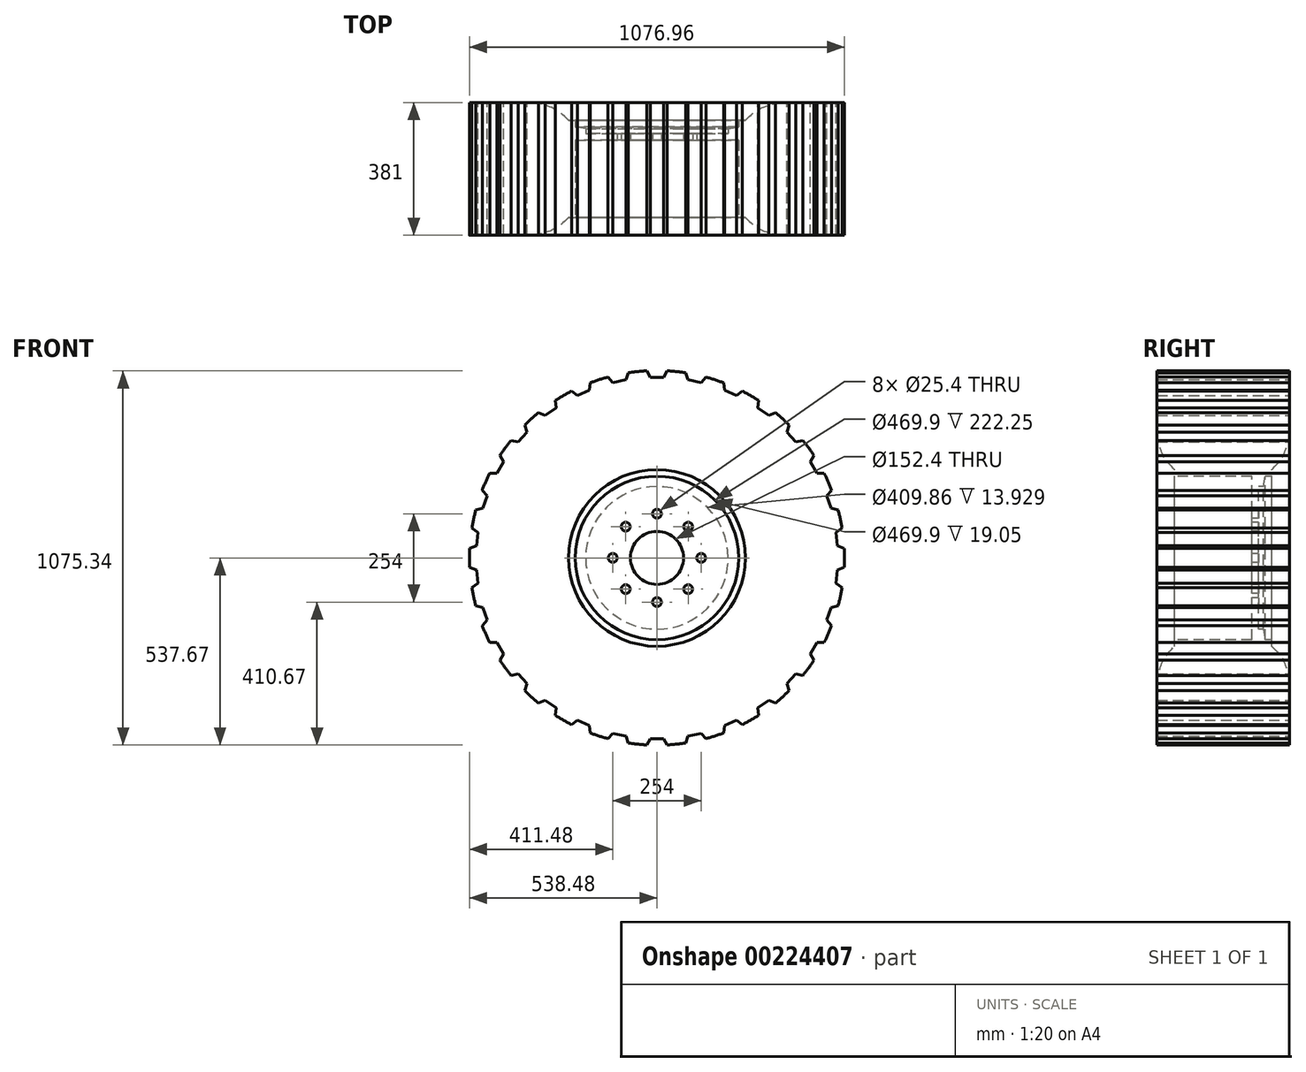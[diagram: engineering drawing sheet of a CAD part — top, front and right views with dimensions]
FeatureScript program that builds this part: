
annotation { "Feature Type Name" : "Feature", "Feature Type Description" : "" }
export const myFeature = defineFeature(function(context is Context, id is Id, definition is map)
    precondition{}
    {
        {
            var Q0;
            Q0=qCreatedBy(makeId("Top.planeOp"),FACE);
            var sketch = newSketch(context, id + "F0", { "sketchPlane" : qUnion([Q0])});
            skLineSegment(sketch, "E0", {"start": v(-538.48, 190.5) * mm, "end": v(-538.48, -190.5) * mm});
            skLineSegment(sketch, "E1", {"start": v(-538.48, -190.5) * mm, "end": v(-367.6, -190.5) * mm});
            skLineSegment(sketch, "E2", {"start": v(-538.48, 190.5) * mm, "end": v(-367.6, 190.5) * mm});
            skLineSegment(sketch, "E3", {"start": v(0, 0) * mm, "end": v(0, 343.31) * mm, "construction": true});
            skArc(sketch, "E4", {"start": v(-254, 139.7) * mm, "mid": v(-305.38, 177.22) * mm, "end": v(-367.6, 190.5) * mm});
            skArc(sketch, "E5", {"start": v(-367.6, -190.5) * mm, "mid": v(-305.38, -177.22) * mm, "end": v(-254, -139.7) * mm});
            skLineSegment(sketch, "E6", {"start": v(0, 0) * mm, "end": v(-538.48, 0) * mm, "construction": true});
            skLineSegment(sketch, "E7", {"start": v(-254, 139.7) * mm, "end": v(-254, -139.7) * mm});
            skLineSegment(sketch, "E8", {"start": v(-254, 139.7) * mm, "end": v(-234.95, 139.7) * mm});
            skLineSegment(sketch, "E9", {"start": v(-234.95, 139.7) * mm, "end": v(-234.95, 101.6) * mm});
            skLineSegment(sketch, "E10", {"start": v(-234.95, 101.6) * mm, "end": v(-76.2, 101.6) * mm});
            skLineSegment(sketch, "E11", {"start": v(-76.2, 101.6) * mm, "end": v(-76.2, 82.55) * mm});
            skLineSegment(sketch, "E12", {"start": v(-76.2, 82.55) * mm, "end": v(-234.95, 82.55) * mm});
            skLineSegment(sketch, "E13", {"start": v(-234.95, 82.55) * mm, "end": v(-234.95, -139.7) * mm});
            skLineSegment(sketch, "E14", {"start": v(-234.95, -139.7) * mm, "end": v(-254, -139.7) * mm});
            skLineSegment(sketch, "E15", {"start": v(-234.95, 120.65) * mm, "end": v(-204.93, 115.53) * mm});
            skLineSegment(sketch, "E16", {"start": v(-204.93, 115.53) * mm, "end": v(-204.93, 101.6) * mm});
            skSolve(sketch);
        }
        {
            var Q0;
            Q0 = qSketchRegion(id + "F0", true);
            var Q1;
            Q1=sQuery(id+"F0.wireOp",EDGE,"E3");
            revolve(context, id + "F1", {"entities" : qUnion([Q0]), "axis" : qUnion([Q1]), "revolveType" : RevolveType.FULL});
        }
        {
            var Q0;
            Q0=makeQuery(id+"F1.opRevolve","SWEPT_FACE",FACE,{"disambiguationData":[OSD([sQuery(id+"F0.wireOp",EDGE,"E1")])]});
            var sketch = newSketch(context, id + "F2", { "sketchPlane" : qUnion([Q0])});
            skCircle(sketch, "E17", {"center": v(0, 127) * mm, "radius": 12.7 * mm});
            skCircle(sketch, "E18.1.0", {"center": v(-89.8, 89.8) * mm, "radius": 12.7 * mm});
            skCircle(sketch, "E18.2.0", {"center": v(-127, 0) * mm, "radius": 12.7 * mm});
            skCircle(sketch, "E18.3.0", {"center": v(-89.8, -89.8) * mm, "radius": 12.7 * mm});
            skCircle(sketch, "E18.4.0", {"center": v(0, -127) * mm, "radius": 12.7 * mm});
            skCircle(sketch, "E18.5.0", {"center": v(89.8, -89.8) * mm, "radius": 12.7 * mm});
            skCircle(sketch, "E18.6.0", {"center": v(127, 0) * mm, "radius": 12.7 * mm});
            skCircle(sketch, "E18.7.0", {"center": v(89.8, 89.8) * mm, "radius": 12.7 * mm});
            skPoint(sketch, "E18.center", {"position": v(0, 0) * mm});
            skSolve(sketch);
        }
        {
            var Q0;
            Q0 = qSketchRegion(id + "F2", true);
            extrude(context, id + "F3", {"entities" : qUnion([Q0]), "operationType" : NewBodyOperationType.REMOVE, "endBound" : BoundingType.THROUGH_ALL, "oppositeDirection" : true, "depth" : 25.4 * mm});
        }
        {
            var Q0;
            Q0=makeQuery(id+"F1.opRevolve","SWEPT_FACE",FACE,{"disambiguationData":[OSD([sQuery(id+"F0.wireOp",EDGE,"E2")])]});
            var sketch = newSketch(context, id + "F4", { "sketchPlane" : qUnion([Q0])});
            skLineSegment(sketch, "E19", {"start": v(-29.58, 537.67) * mm, "end": v(-19.05, 519.43) * mm});
            skLineSegment(sketch, "E20", {"start": v(-19.05, 519.43) * mm, "end": v(19.05, 519.43) * mm});
            skLineSegment(sketch, "E21", {"start": v(19.05, 519.43) * mm, "end": v(29.58, 537.67) * mm});
            skArc(sketch, "E22.0", {"start": v(29.58, 537.67) * mm, "mid": v(0, 538.48) * mm, "end": v(-29.58, 537.67) * mm});
            skLineSegment(sketch, "E23", {"start": v(0, 519.43) * mm, "end": v(0, 0) * mm, "construction": true});
            skLineSegment(sketch, "E24.1.0", {"start": v(-140.72, 519.77) * mm, "end": v(-126.63, 504.12) * mm});
            skLineSegment(sketch, "E24.1.1", {"start": v(-126.63, 504.12) * mm, "end": v(-89.36, 512.04) * mm});
            skLineSegment(sketch, "E24.1.2", {"start": v(-89.36, 512.04) * mm, "end": v(-82.85, 532.07) * mm});
            skArc(sketch, "E24.1.3", {"start": v(-82.85, 532.07) * mm, "mid": v(-111.96, 526.71) * mm, "end": v(-140.72, 519.77) * mm});
            skLineSegment(sketch, "E24.2.0", {"start": v(-245.71, 479.15) * mm, "end": v(-228.67, 466.77) * mm});
            skLineSegment(sketch, "E24.2.1", {"start": v(-228.67, 466.77) * mm, "end": v(-193.87, 482.27) * mm});
            skLineSegment(sketch, "E24.2.2", {"start": v(-193.87, 482.27) * mm, "end": v(-191.67, 503.21) * mm});
            skArc(sketch, "E24.2.3", {"start": v(-191.67, 503.21) * mm, "mid": v(-219.02, 491.93) * mm, "end": v(-245.71, 479.15) * mm});
            skLineSegment(sketch, "E24.3.0", {"start": v(-339.96, 417.6) * mm, "end": v(-320.73, 409.03) * mm});
            skLineSegment(sketch, "E24.3.1", {"start": v(-320.73, 409.03) * mm, "end": v(-289.9, 431.43) * mm});
            skLineSegment(sketch, "E24.3.2", {"start": v(-289.9, 431.43) * mm, "end": v(-292.1, 452.37) * mm});
            skArc(sketch, "E24.3.3", {"start": v(-292.1, 452.37) * mm, "mid": v(-316.51, 435.64) * mm, "end": v(-339.96, 417.6) * mm});
            skLineSegment(sketch, "E24.4.0", {"start": v(-419.36, 337.79) * mm, "end": v(-398.76, 333.4) * mm});
            skLineSegment(sketch, "E24.4.1", {"start": v(-398.76, 333.4) * mm, "end": v(-373.26, 361.72) * mm});
            skLineSegment(sketch, "E24.4.2", {"start": v(-373.26, 361.72) * mm, "end": v(-379.77, 381.75) * mm});
            skArc(sketch, "E24.4.3", {"start": v(-379.77, 381.75) * mm, "mid": v(-400.17, 360.31) * mm, "end": v(-419.36, 337.79) * mm});
            skLineSegment(sketch, "E24.5.0", {"start": v(-480.42, 243.22) * mm, "end": v(-459.36, 243.22) * mm});
            skLineSegment(sketch, "E24.5.1", {"start": v(-459.36, 243.22) * mm, "end": v(-440.31, 276.21) * mm});
            skLineSegment(sketch, "E24.5.2", {"start": v(-440.31, 276.21) * mm, "end": v(-450.84, 294.45) * mm});
            skArc(sketch, "E24.5.3", {"start": v(-450.84, 294.45) * mm, "mid": v(-466.34, 269.24) * mm, "end": v(-480.42, 243.22) * mm});
            skLineSegment(sketch, "E24.6.0", {"start": v(-520.5, 138.02) * mm, "end": v(-499.9, 142.4) * mm});
            skLineSegment(sketch, "E24.6.1", {"start": v(-499.9, 142.4) * mm, "end": v(-488.12, 178.63) * mm});
            skLineSegment(sketch, "E24.6.2", {"start": v(-488.12, 178.63) * mm, "end": v(-502.21, 194.28) * mm});
            skArc(sketch, "E24.6.3", {"start": v(-502.21, 194.28) * mm, "mid": v(-512.12, 166.4) * mm, "end": v(-520.5, 138.02) * mm});
            skLineSegment(sketch, "E24.7.0", {"start": v(-537.81, 26.78) * mm, "end": v(-518.58, 35.35) * mm});
            skLineSegment(sketch, "E24.7.1", {"start": v(-518.58, 35.35) * mm, "end": v(-514.6, 73.24) * mm});
            skLineSegment(sketch, "E24.7.2", {"start": v(-514.6, 73.24) * mm, "end": v(-531.63, 85.62) * mm});
            skArc(sketch, "E24.7.3", {"start": v(-531.63, 85.62) * mm, "mid": v(-535.53, 56.29) * mm, "end": v(-537.81, 26.78) * mm});
            skLineSegment(sketch, "E24.8.0", {"start": v(-531.63, -85.62) * mm, "end": v(-514.6, -73.24) * mm});
            skLineSegment(sketch, "E24.8.1", {"start": v(-514.6, -73.24) * mm, "end": v(-518.58, -35.35) * mm});
            skLineSegment(sketch, "E24.8.2", {"start": v(-518.58, -35.35) * mm, "end": v(-537.81, -26.78) * mm});
            skArc(sketch, "E24.8.3", {"start": v(-537.81, -26.78) * mm, "mid": v(-535.53, -56.29) * mm, "end": v(-531.63, -85.62) * mm});
            skLineSegment(sketch, "E24.9.0", {"start": v(-502.21, -194.28) * mm, "end": v(-488.12, -178.63) * mm});
            skLineSegment(sketch, "E24.9.1", {"start": v(-488.12, -178.63) * mm, "end": v(-499.9, -142.4) * mm});
            skLineSegment(sketch, "E24.9.2", {"start": v(-499.9, -142.4) * mm, "end": v(-520.5, -138.02) * mm});
            skArc(sketch, "E24.9.3", {"start": v(-520.5, -138.02) * mm, "mid": v(-512.12, -166.4) * mm, "end": v(-502.21, -194.28) * mm});
            skLineSegment(sketch, "E24.10.0", {"start": v(-450.84, -294.45) * mm, "end": v(-440.31, -276.21) * mm});
            skLineSegment(sketch, "E24.10.1", {"start": v(-440.31, -276.21) * mm, "end": v(-459.36, -243.22) * mm});
            skLineSegment(sketch, "E24.10.2", {"start": v(-459.36, -243.22) * mm, "end": v(-480.42, -243.22) * mm});
            skArc(sketch, "E24.10.3", {"start": v(-480.42, -243.22) * mm, "mid": v(-466.34, -269.24) * mm, "end": v(-450.84, -294.45) * mm});
            skLineSegment(sketch, "E24.11.0", {"start": v(-379.77, -381.75) * mm, "end": v(-373.26, -361.72) * mm});
            skLineSegment(sketch, "E24.11.1", {"start": v(-373.26, -361.72) * mm, "end": v(-398.76, -333.4) * mm});
            skLineSegment(sketch, "E24.11.2", {"start": v(-398.76, -333.4) * mm, "end": v(-419.36, -337.79) * mm});
            skArc(sketch, "E24.11.3", {"start": v(-419.36, -337.79) * mm, "mid": v(-400.17, -360.31) * mm, "end": v(-379.77, -381.75) * mm});
            skLineSegment(sketch, "E24.12.0", {"start": v(-292.1, -452.37) * mm, "end": v(-289.9, -431.43) * mm});
            skLineSegment(sketch, "E24.12.1", {"start": v(-289.9, -431.43) * mm, "end": v(-320.73, -409.03) * mm});
            skLineSegment(sketch, "E24.12.2", {"start": v(-320.73, -409.03) * mm, "end": v(-339.96, -417.6) * mm});
            skArc(sketch, "E24.12.3", {"start": v(-339.96, -417.6) * mm, "mid": v(-316.51, -435.64) * mm, "end": v(-292.1, -452.37) * mm});
            skLineSegment(sketch, "E24.13.0", {"start": v(-191.67, -503.21) * mm, "end": v(-193.87, -482.27) * mm});
            skLineSegment(sketch, "E24.13.1", {"start": v(-193.87, -482.27) * mm, "end": v(-228.67, -466.77) * mm});
            skLineSegment(sketch, "E24.13.2", {"start": v(-228.67, -466.77) * mm, "end": v(-245.71, -479.15) * mm});
            skArc(sketch, "E24.13.3", {"start": v(-245.71, -479.15) * mm, "mid": v(-219.02, -491.93) * mm, "end": v(-191.67, -503.21) * mm});
            skLineSegment(sketch, "E24.14.0", {"start": v(-82.85, -532.07) * mm, "end": v(-89.36, -512.04) * mm});
            skLineSegment(sketch, "E24.14.1", {"start": v(-89.36, -512.04) * mm, "end": v(-126.63, -504.12) * mm});
            skLineSegment(sketch, "E24.14.2", {"start": v(-126.63, -504.12) * mm, "end": v(-140.72, -519.77) * mm});
            skArc(sketch, "E24.14.3", {"start": v(-140.72, -519.77) * mm, "mid": v(-111.96, -526.71) * mm, "end": v(-82.85, -532.07) * mm});
            skLineSegment(sketch, "E24.15.0", {"start": v(29.58, -537.67) * mm, "end": v(19.05, -519.43) * mm});
            skLineSegment(sketch, "E24.15.1", {"start": v(19.05, -519.43) * mm, "end": v(-19.05, -519.43) * mm});
            skLineSegment(sketch, "E24.15.2", {"start": v(-19.05, -519.43) * mm, "end": v(-29.58, -537.67) * mm});
            skArc(sketch, "E24.15.3", {"start": v(-29.58, -537.67) * mm, "mid": v(0, -538.48) * mm, "end": v(29.58, -537.67) * mm});
            skLineSegment(sketch, "E24.16.0", {"start": v(140.72, -519.77) * mm, "end": v(126.63, -504.12) * mm});
            skLineSegment(sketch, "E24.16.1", {"start": v(126.63, -504.12) * mm, "end": v(89.36, -512.04) * mm});
            skLineSegment(sketch, "E24.16.2", {"start": v(89.36, -512.04) * mm, "end": v(82.85, -532.07) * mm});
            skArc(sketch, "E24.16.3", {"start": v(82.85, -532.07) * mm, "mid": v(111.96, -526.71) * mm, "end": v(140.72, -519.77) * mm});
            skLineSegment(sketch, "E24.17.0", {"start": v(245.71, -479.15) * mm, "end": v(228.67, -466.77) * mm});
            skLineSegment(sketch, "E24.17.1", {"start": v(228.67, -466.77) * mm, "end": v(193.87, -482.27) * mm});
            skLineSegment(sketch, "E24.17.2", {"start": v(193.87, -482.27) * mm, "end": v(191.67, -503.21) * mm});
            skArc(sketch, "E24.17.3", {"start": v(191.67, -503.21) * mm, "mid": v(219.02, -491.93) * mm, "end": v(245.71, -479.15) * mm});
            skLineSegment(sketch, "E24.18.0", {"start": v(339.96, -417.6) * mm, "end": v(320.73, -409.03) * mm});
            skLineSegment(sketch, "E24.18.1", {"start": v(320.73, -409.03) * mm, "end": v(289.9, -431.43) * mm});
            skLineSegment(sketch, "E24.18.2", {"start": v(289.9, -431.43) * mm, "end": v(292.1, -452.37) * mm});
            skArc(sketch, "E24.18.3", {"start": v(292.1, -452.37) * mm, "mid": v(316.51, -435.64) * mm, "end": v(339.96, -417.6) * mm});
            skLineSegment(sketch, "E24.19.0", {"start": v(419.36, -337.79) * mm, "end": v(398.76, -333.4) * mm});
            skLineSegment(sketch, "E24.19.1", {"start": v(398.76, -333.4) * mm, "end": v(373.26, -361.72) * mm});
            skLineSegment(sketch, "E24.19.2", {"start": v(373.26, -361.72) * mm, "end": v(379.77, -381.75) * mm});
            skArc(sketch, "E24.19.3", {"start": v(379.77, -381.75) * mm, "mid": v(400.17, -360.31) * mm, "end": v(419.36, -337.79) * mm});
            skLineSegment(sketch, "E24.20.0", {"start": v(480.42, -243.22) * mm, "end": v(459.36, -243.22) * mm});
            skLineSegment(sketch, "E24.20.1", {"start": v(459.36, -243.22) * mm, "end": v(440.31, -276.21) * mm});
            skLineSegment(sketch, "E24.20.2", {"start": v(440.31, -276.21) * mm, "end": v(450.84, -294.45) * mm});
            skArc(sketch, "E24.20.3", {"start": v(450.84, -294.45) * mm, "mid": v(466.34, -269.24) * mm, "end": v(480.42, -243.22) * mm});
            skLineSegment(sketch, "E24.21.0", {"start": v(520.5, -138.02) * mm, "end": v(499.9, -142.4) * mm});
            skLineSegment(sketch, "E24.21.1", {"start": v(499.9, -142.4) * mm, "end": v(488.12, -178.63) * mm});
            skLineSegment(sketch, "E24.21.2", {"start": v(488.12, -178.63) * mm, "end": v(502.21, -194.28) * mm});
            skArc(sketch, "E24.21.3", {"start": v(502.21, -194.28) * mm, "mid": v(512.12, -166.4) * mm, "end": v(520.5, -138.02) * mm});
            skLineSegment(sketch, "E24.22.0", {"start": v(537.81, -26.78) * mm, "end": v(518.58, -35.35) * mm});
            skLineSegment(sketch, "E24.22.1", {"start": v(518.58, -35.35) * mm, "end": v(514.6, -73.24) * mm});
            skLineSegment(sketch, "E24.22.2", {"start": v(514.6, -73.24) * mm, "end": v(531.63, -85.62) * mm});
            skArc(sketch, "E24.22.3", {"start": v(531.63, -85.62) * mm, "mid": v(535.53, -56.29) * mm, "end": v(537.81, -26.78) * mm});
            skLineSegment(sketch, "E24.23.0", {"start": v(531.63, 85.62) * mm, "end": v(514.6, 73.24) * mm});
            skLineSegment(sketch, "E24.23.1", {"start": v(514.6, 73.24) * mm, "end": v(518.58, 35.35) * mm});
            skLineSegment(sketch, "E24.23.2", {"start": v(518.58, 35.35) * mm, "end": v(537.81, 26.78) * mm});
            skArc(sketch, "E24.23.3", {"start": v(537.81, 26.78) * mm, "mid": v(535.53, 56.29) * mm, "end": v(531.63, 85.62) * mm});
            skLineSegment(sketch, "E24.24.0", {"start": v(502.21, 194.28) * mm, "end": v(488.12, 178.63) * mm});
            skLineSegment(sketch, "E24.24.1", {"start": v(488.12, 178.63) * mm, "end": v(499.9, 142.4) * mm});
            skLineSegment(sketch, "E24.24.2", {"start": v(499.9, 142.4) * mm, "end": v(520.5, 138.02) * mm});
            skArc(sketch, "E24.24.3", {"start": v(520.5, 138.02) * mm, "mid": v(512.12, 166.4) * mm, "end": v(502.21, 194.28) * mm});
            skLineSegment(sketch, "E24.25.0", {"start": v(450.84, 294.45) * mm, "end": v(440.31, 276.21) * mm});
            skLineSegment(sketch, "E24.25.1", {"start": v(440.31, 276.21) * mm, "end": v(459.36, 243.22) * mm});
            skLineSegment(sketch, "E24.25.2", {"start": v(459.36, 243.22) * mm, "end": v(480.42, 243.22) * mm});
            skArc(sketch, "E24.25.3", {"start": v(480.42, 243.22) * mm, "mid": v(466.34, 269.24) * mm, "end": v(450.84, 294.45) * mm});
            skLineSegment(sketch, "E24.26.0", {"start": v(379.77, 381.75) * mm, "end": v(373.26, 361.72) * mm});
            skLineSegment(sketch, "E24.26.1", {"start": v(373.26, 361.72) * mm, "end": v(398.76, 333.4) * mm});
            skLineSegment(sketch, "E24.26.2", {"start": v(398.76, 333.4) * mm, "end": v(419.36, 337.79) * mm});
            skArc(sketch, "E24.26.3", {"start": v(419.36, 337.79) * mm, "mid": v(400.17, 360.31) * mm, "end": v(379.77, 381.75) * mm});
            skLineSegment(sketch, "E24.27.0", {"start": v(292.1, 452.37) * mm, "end": v(289.9, 431.43) * mm});
            skLineSegment(sketch, "E24.27.1", {"start": v(289.9, 431.43) * mm, "end": v(320.73, 409.03) * mm});
            skLineSegment(sketch, "E24.27.2", {"start": v(320.73, 409.03) * mm, "end": v(339.96, 417.6) * mm});
            skArc(sketch, "E24.27.3", {"start": v(339.96, 417.6) * mm, "mid": v(316.51, 435.64) * mm, "end": v(292.1, 452.37) * mm});
            skLineSegment(sketch, "E24.28.0", {"start": v(191.67, 503.21) * mm, "end": v(193.87, 482.27) * mm});
            skLineSegment(sketch, "E24.28.1", {"start": v(193.87, 482.27) * mm, "end": v(228.67, 466.77) * mm});
            skLineSegment(sketch, "E24.28.2", {"start": v(228.67, 466.77) * mm, "end": v(245.71, 479.15) * mm});
            skArc(sketch, "E24.28.3", {"start": v(245.71, 479.15) * mm, "mid": v(219.02, 491.93) * mm, "end": v(191.67, 503.21) * mm});
            skLineSegment(sketch, "E24.29.0", {"start": v(82.85, 532.07) * mm, "end": v(89.36, 512.04) * mm});
            skLineSegment(sketch, "E24.29.1", {"start": v(89.36, 512.04) * mm, "end": v(126.63, 504.12) * mm});
            skLineSegment(sketch, "E24.29.2", {"start": v(126.63, 504.12) * mm, "end": v(140.72, 519.77) * mm});
            skArc(sketch, "E24.29.3", {"start": v(140.72, 519.77) * mm, "mid": v(111.96, 526.71) * mm, "end": v(82.85, 532.07) * mm});
            skSolve(sketch);
        }
        {
            var Q0;
            Q0 = qSketchRegion(id + "F4", true);
            extrude(context, id + "F5", {"entities" : qUnion([Q0]), "operationType" : NewBodyOperationType.REMOVE, "endBound" : BoundingType.THROUGH_ALL, "oppositeDirection" : true, "depth" : 25.4 * mm});
        }
    });
